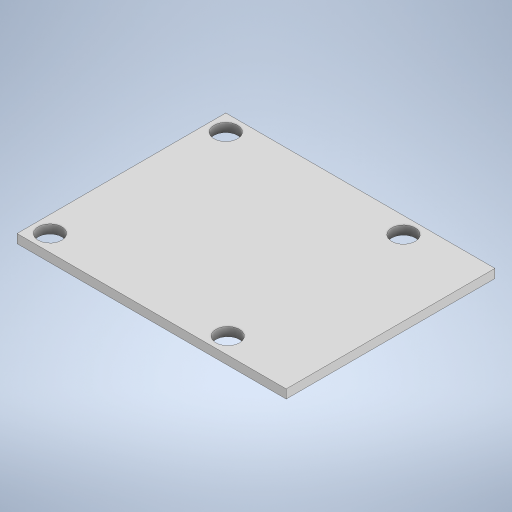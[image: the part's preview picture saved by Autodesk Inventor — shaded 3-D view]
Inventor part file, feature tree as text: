
AUTODESK INVENTOR PART (.ipt)
format: ipt  version: 2023.2 (Build 272271000, 271)  size: 222,208 bytes
history: native  units: in
note: dims shown in document units (in); Inventor stores cm internally (conversion verified against a paired STEP export)
features: sketch x2, extrude x1, hole x1
ambient origin geometry x8: Origin, YZ Plane, XZ Plane, XY Plane, X Axis, Y Axis, Z Axis, Center Point
bodies: Solid1 (feature_tree)
feature tree (4):
  extrude  "Extrusion1"  Depth=1.9291in
  hole  "Hole1"  [1 undecoded]
  sketch  "Sketch1"  dims[d0=1.4961in d1=1.9291in]
  sketch  "Sketch2"  dims[d2=0.063in d3=0.0in d5=1.2736in d6=0.1181in d7=0.1695in d8=0.2362in d9=0.279in d10=0.0984in d11=0.5635in d12=0.315in d13=0.8108in d14=0.1181in]
note: 1 required parameter value undecoded (feature->parameter linkage not recoverable at this tier; creation-order binding heuristic only, values carry confidence <= 0.55)
